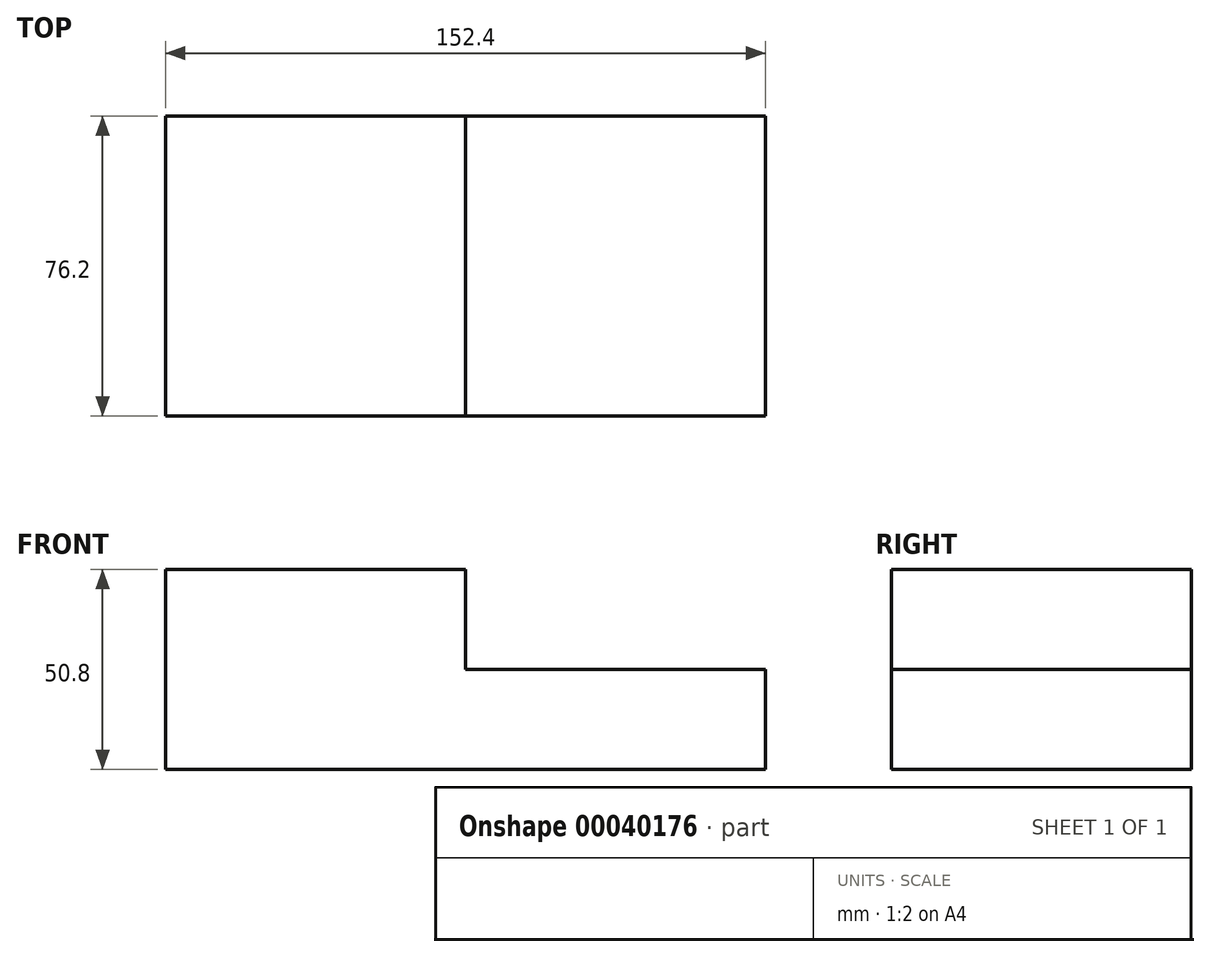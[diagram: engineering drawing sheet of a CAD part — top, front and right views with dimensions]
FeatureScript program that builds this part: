
annotation { "Feature Type Name" : "Feature", "Feature Type Description" : "" }
export const myFeature = defineFeature(function(context is Context, id is Id, definition is map)
    precondition{}
    {
        {
            var Q0;
            Q0=qCreatedBy(makeId("Top.planeOp"),FACE);
            var sketch = newSketch(context, id + "F0", { "sketchPlane" : qUnion([Q0])});
            skLineSegment(sketch, "E0.bottom", {"start": v(-90.28, -33.91) * mm, "end": v(62.12, -33.91) * mm});
            skLineSegment(sketch, "E0.top", {"start": v(-90.28, 42.29) * mm, "end": v(62.12, 42.29) * mm});
            skLineSegment(sketch, "E0.left", {"start": v(-90.28, -33.91) * mm, "end": v(-90.28, 42.29) * mm});
            skLineSegment(sketch, "E0.right", {"start": v(62.12, -33.91) * mm, "end": v(62.12, 42.29) * mm});
            skSolve(sketch);
        }
        {
            var Q0;
            Q0 = qSketchRegion(id + "F0", true);
            extrude(context, id + "F1", {"entities" : qUnion([Q0]), "depth" : 25.4 * mm});
        }
        {
            var Q0;
            Q0=makeQuery(id+"F1.opExtrude","CAP_FACE",FACE,{"disambiguationData":[OSD([sQuery(id+"F0.wireOp",EDGE,"E0.bottom"),sQuery(id+"F0.wireOp",EDGE,"E0.top"),sQuery(id+"F0.wireOp",EDGE,"E0.left"),sQuery(id+"F0.wireOp",EDGE,"E0.right")])],"isStart":false});
            var sketch = newSketch(context, id + "F2", { "sketchPlane" : qUnion([Q0])});
            skLineSegment(sketch, "E1.bottom", {"start": v(-90.28, -33.91) * mm, "end": v(-14.08, -33.91) * mm});
            skLineSegment(sketch, "E1.top", {"start": v(-90.28, 42.29) * mm, "end": v(-14.08, 42.29) * mm});
            skLineSegment(sketch, "E1.left", {"start": v(-90.28, -33.91) * mm, "end": v(-90.28, 42.29) * mm});
            skLineSegment(sketch, "E1.right", {"start": v(-14.08, -33.91) * mm, "end": v(-14.08, 42.29) * mm});
            skSolve(sketch);
        }
        {
            var Q0;
            Q0 = qSketchRegion(id + "F2", true);
            extrude(context, id + "F3", {"entities" : qUnion([Q0]), "operationType" : NewBodyOperationType.ADD, "depth" : 25.4 * mm});
        }
    });
